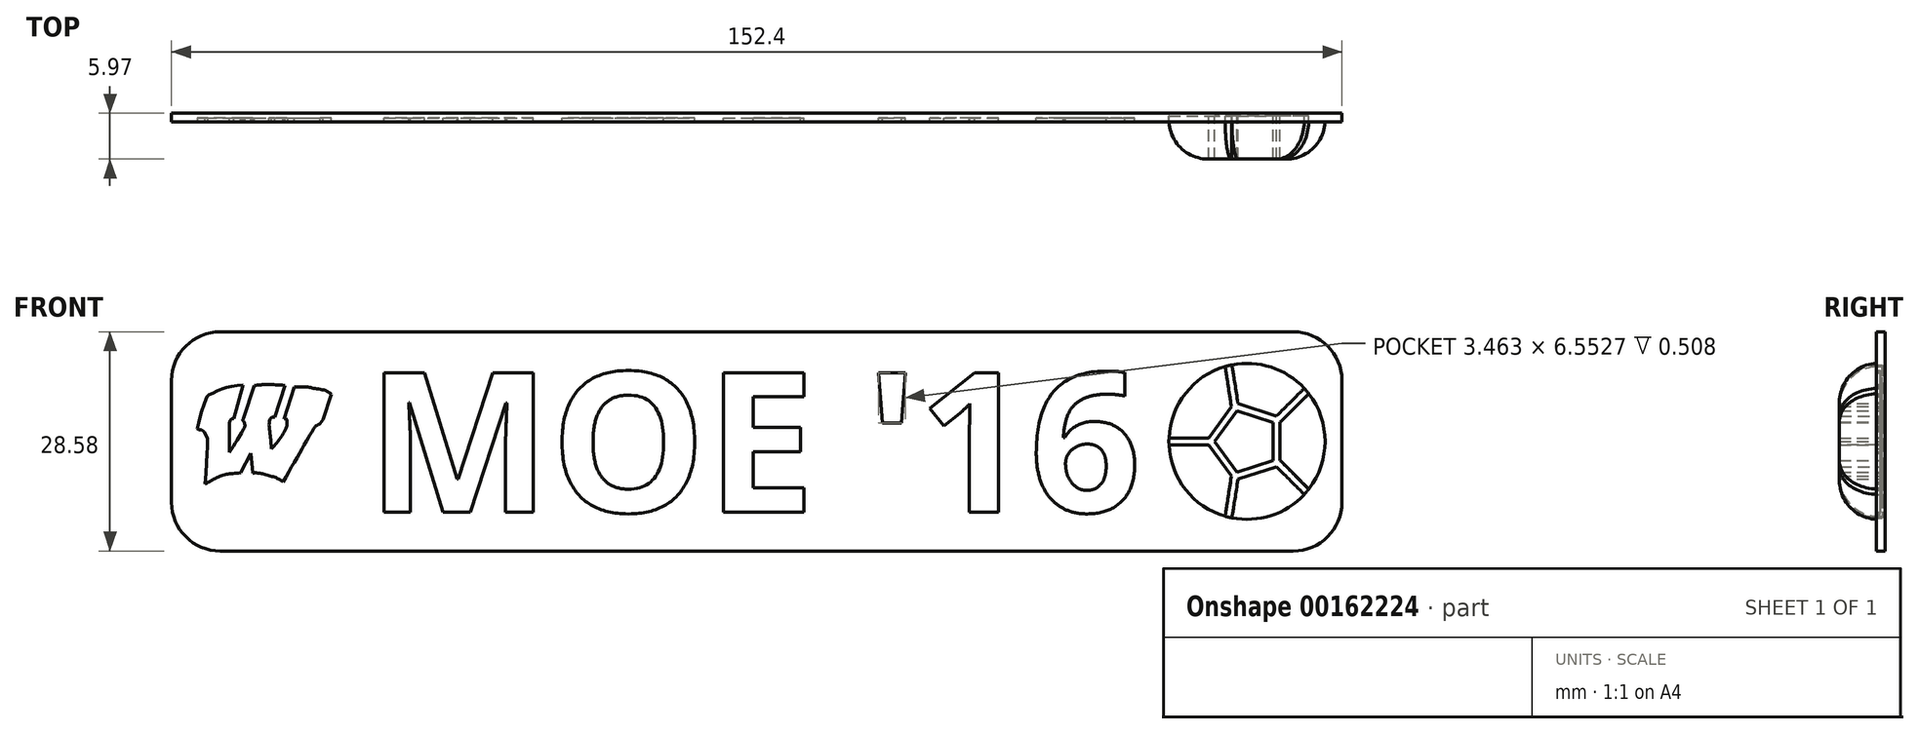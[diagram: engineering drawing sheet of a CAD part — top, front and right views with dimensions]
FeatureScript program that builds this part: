
annotation { "Feature Type Name" : "Feature", "Feature Type Description" : "" }
export const myFeature = defineFeature(function(context is Context, id is Id, definition is map)
    precondition{}
    {
        {
            var Q0;
            Q0=qCreatedBy(makeId("Front.planeOp"),FACE);
            var sketch = newSketch(context, id + "F0", { "sketchPlane" : qUnion([Q0])});
            skLineSegment(sketch, "E0.bottom", {"start": v(-52.2, 14.29) * mm, "end": v(87.5, 14.29) * mm});
            skLineSegment(sketch, "E0.top", {"start": v(-52.2, -14.29) * mm, "end": v(87.5, -14.29) * mm});
            skLineSegment(sketch, "E0.left", {"start": v(-58.55, 7.94) * mm, "end": v(-58.55, -7.94) * mm});
            skLineSegment(sketch, "E0.right", {"start": v(93.85, 7.94) * mm, "end": v(93.85, -7.94) * mm});
            skText(sketch, "E1", { "text": "MOE \'16", "fontName": "OpenSans-Bold.ttf"});
            skCircle(sketch, "E2", {"center": v(81.48, 0) * mm, "radius": 10.16 * mm});
            skCircle(sketch, "E3.cCircle", {"center": v(81.48, 0) * mm, "radius": 3.4 * mm, "construction": true});
            skLineSegment(sketch, "E3.0", {"start": v(84.88, 2.47) * mm, "end": v(84.88, -2.47) * mm});
            skLineSegment(sketch, "E3.1", {"start": v(84.88, -2.47) * mm, "end": v(80.18, -4) * mm});
            skLineSegment(sketch, "E3.2", {"start": v(80.18, -4) * mm, "end": v(77.27, 0) * mm});
            skLineSegment(sketch, "E3.3", {"start": v(77.27, 0) * mm, "end": v(80.18, 4) * mm});
            skLineSegment(sketch, "E3.4", {"start": v(80.18, 4) * mm, "end": v(84.88, 2.47) * mm});
            skPoint(sketch, "E3.0.midPoint", {"position": v(84.88, 0) * mm});
            skCircle(sketch, "E4.cCircle", {"center": v(81.48, 0) * mm, "radius": 4.32 * mm, "construction": true});
            skLineSegment(sketch, "E4.0", {"start": v(85.8, 3.14) * mm, "end": v(85.8, -3.14) * mm});
            skLineSegment(sketch, "E4.1", {"start": v(85.8, -3.14) * mm, "end": v(79.83, -5.08) * mm});
            skLineSegment(sketch, "E4.2", {"start": v(79.83, -5.08) * mm, "end": v(76.14, 0) * mm});
            skLineSegment(sketch, "E4.3", {"start": v(76.14, 0) * mm, "end": v(79.83, 5.08) * mm});
            skLineSegment(sketch, "E4.4", {"start": v(79.83, 5.08) * mm, "end": v(85.8, 3.14) * mm});
            skPoint(sketch, "E4.0.midPoint", {"position": v(85.8, 0) * mm});
            skLineSegment(sketch, "E5", {"start": v(85.8, 3.14) * mm, "end": v(89.23, 6.57) * mm, "construction": true});
            skLineSegment(sketch, "E6", {"start": v(85.8, -3.14) * mm, "end": v(89.23, -6.57) * mm, "construction": true});
            skLineSegment(sketch, "E7", {"start": v(76.14, 0) * mm, "end": v(71.32, 0) * mm, "construction": true});
            skLineSegment(sketch, "E8", {"start": v(79.83, 5.08) * mm, "end": v(79.07, 9.88) * mm, "construction": true});
            skLineSegment(sketch, "E9", {"start": v(79.83, -5.08) * mm, "end": v(79.07, -9.88) * mm, "construction": true});
            skLineSegment(sketch, "E10", {"start": v(79.45, 4.55) * mm, "end": v(78.63, 9.76) * mm});
            skLineSegment(sketch, "E11", {"start": v(79.52, 9.97) * mm, "end": v(80.32, 4.92) * mm});
            skLineSegment(sketch, "E12", {"start": v(71.33, 0.46) * mm, "end": v(76.48, 0.46) * mm});
            skLineSegment(sketch, "E13", {"start": v(71.33, -0.46) * mm, "end": v(76.48, -0.46) * mm});
            skLineSegment(sketch, "E14", {"start": v(79.45, -4.55) * mm, "end": v(78.63, -9.76) * mm});
            skPoint(sketch, "E14.startSnap0", {"position": v(79.45, -7.48) * mm});
            skLineSegment(sketch, "E15", {"start": v(80.32, -4.92) * mm, "end": v(79.52, -9.97) * mm});
            skLineSegment(sketch, "E16", {"start": v(88.93, -6.92) * mm, "end": v(85.31, -3.3) * mm});
            skLineSegment(sketch, "E17", {"start": v(89.52, -6.22) * mm, "end": v(85.8, -2.5) * mm});
            skLineSegment(sketch, "E18", {"start": v(85.8, 2.5) * mm, "end": v(89.52, 6.22) * mm});
            skLineSegment(sketch, "E19", {"start": v(85.31, 3.3) * mm, "end": v(88.93, 6.92) * mm});
            skPoint(sketch, "E20.visualSharp", {"position": v(93.85, 14.29) * mm});
            skArc(sketch, "E20.filletArc", {"start": v(93.85, 7.94) * mm, "mid": v(92, 12.43) * mm, "end": v(87.5, 14.29) * mm});
            skPoint(sketch, "E21.visualSharp", {"position": v(93.85, -14.29) * mm});
            skArc(sketch, "E21.filletArc", {"start": v(87.5, -14.29) * mm, "mid": v(92, -12.43) * mm, "end": v(93.85, -7.94) * mm});
            skPoint(sketch, "E22.visualSharp", {"position": v(-58.55, 14.29) * mm});
            skArc(sketch, "E22.filletArc", {"start": v(-52.2, 14.29) * mm, "mid": v(-56.69, 12.43) * mm, "end": v(-58.55, 7.94) * mm});
            skPoint(sketch, "E23.visualSharp", {"position": v(-58.55, -14.29) * mm});
            skArc(sketch, "E23.filletArc", {"start": v(-58.55, -7.94) * mm, "mid": v(-56.69, -12.43) * mm, "end": v(-52.2, -14.29) * mm});
            skFitSpline(sketch, "E24", {"points": [v(-49.22, 7.36) * mm, v(-51.14, 7.07) * mm, v(-52.41, 6.66) * mm, v(-53.63, 6.08) * mm, v(-54.04, 5.65) * mm, v(-55.17, 1.56) * mm, v(-55.05, 1.53) * mm, v(-54.68, 1.5) * mm, v(-54.21, 1.1) * mm, v(-53.9, 0.34) * mm, v(-53.86, -0.6) * mm, v(-54.17, -5.57) * mm], "startDerivative": vector(-18.16, -2.3) * mm, "endDerivative": vector(-2.14, -33.25) * mm});
            skFitSpline(sketch, "E25", {"points": [v(-54.17, -5.57) * mm, v(-53.65, -5.26) * mm, v(-53.07, -4.93) * mm, v(-52.29, -4.57) * mm, v(-51.44, -4.3) * mm, v(-50.68, -4.19) * mm, v(-49.58, -4.1) * mm], "startDerivative": vector(3.4, 2.8) * mm, "endDerivative": vector(6, 0.4) * mm});
            skLineSegment(sketch, "E26", {"start": v(-49.58, -4.1) * mm, "end": v(-48.22, -1.53) * mm});
            skLineSegment(sketch, "E27", {"start": v(-48.22, -1.53) * mm, "end": v(-47.98, -4.12) * mm});
            skFitSpline(sketch, "E28", {"points": [v(-47.98, -4.12) * mm, v(-47.32, -4.12) * mm, v(-46.58, -4.24) * mm, v(-45.54, -4.54) * mm, v(-44.68, -4.86) * mm, v(-44.02, -5.28) * mm], "startDerivative": vector(3.67, 0.12) * mm, "endDerivative": vector(3.24, -2.36) * mm});
            skFitSpline(sketch, "E29", {"points": [v(-44.02, -5.28) * mm, v(-39.97, 1.74) * mm, v(-39.73, 2.03) * mm, v(-39.46, 2.18) * mm, v(-39.19, 2.35) * mm], "startDerivative": vector(8.56, 15.03) * mm, "endDerivative": vector(2.11, 1.44) * mm});
            skLineSegment(sketch, "E30", {"start": v(-39.19, 2.35) * mm, "end": v(-38.85, 2.82) * mm});
            skLineSegment(sketch, "E31", {"start": v(-38.85, 2.82) * mm, "end": v(-37.74, 6.16) * mm});
            skLineSegment(sketch, "E32", {"start": v(-42.55, 7.06) * mm, "end": v(-43.92, 2.93) * mm});
            skLineSegment(sketch, "E33", {"start": v(-43.78, 7.27) * mm, "end": v(-45.08, 3.15) * mm});
            skLineSegment(sketch, "E34", {"start": v(-49.22, 7.36) * mm, "end": v(-50.44, 2.95) * mm});
            skLineSegment(sketch, "E35", {"start": v(-47.78, 7.27) * mm, "end": v(-49.17, 3.01) * mm});
            skLineSegment(sketch, "E36", {"start": v(-51, 2.4) * mm, "end": v(-51, -1.44) * mm});
            skFitSpline(sketch, "E37", {"points": [v(-51, 2.4) * mm, v(-50.93, 2.7) * mm, v(-50.79, 2.86) * mm, v(-50.62, 2.96) * mm, v(-50.44, 2.95) * mm], "startDerivative": vector(0.1, 1.13) * mm, "endDerivative": vector(0.8, -0.18) * mm});
            skFitSpline(sketch, "E38", {"points": [v(-51, -1.44) * mm, v(-49.08, 1.76) * mm, v(-49, 2.04) * mm, v(-49.03, 2.3) * mm, v(-49.22, 2.68) * mm, v(-49.28, 2.8) * mm, v(-49.17, 3.01) * mm], "startDerivative": vector(5.88, 9.47) * mm, "endDerivative": vector(1.55, 2.17) * mm});
            skFitSpline(sketch, "E39", {"points": [v(-45.08, 3.15) * mm, v(-45.28, 3.15) * mm, v(-45.41, 3.15) * mm, v(-45.76, 2.8) * mm, v(-45.7, 0.74) * mm, v(-45.53, -0.95) * mm], "startDerivative": vector(-1.81, -0.11) * mm, "endDerivative": vector(0.55, -5.24) * mm});
            skFitSpline(sketch, "E40", {"points": [v(-43.92, 2.93) * mm, v(-43.6, 2.93) * mm, v(-43.49, 2.47) * mm, v(-43.57, 1.85) * mm, v(-44.45, 0.32) * mm, v(-45.53, -0.95) * mm], "startDerivative": vector(2.79, 0.73) * mm, "endDerivative": vector(-3.92, -4.22) * mm});
            skFitSpline(sketch, "E41", {"points": [v(-47.78, 7.27) * mm, v(-46.38, 7.39) * mm, v(-43.78, 7.27) * mm], "startDerivative": vector(4.88, 0.78) * mm, "endDerivative": vector(4.26, -0.68) * mm});
            skFitSpline(sketch, "E42", {"points": [v(-42.55, 7.06) * mm, v(-40.8, 7.08) * mm, v(-39.86, 6.9) * mm, v(-38.5, 6.61) * mm, v(-37.74, 6.16) * mm], "startDerivative": vector(10.06, 0.33) * mm, "endDerivative": vector(3.23, -2.15) * mm});
            const initialGuessF0  = {"E1": [-0.03315, -0.0092, 1, 0, 0.0183]};
            skSetInitialGuess(sketch, initialGuessF0);
            skSolve(sketch);
        }
        {
            var Q0;
            Q0 = qSketchRegion(id + "F0", true);
            var Q1;
            Q1=makeQuery(id+"F0.imprint","IMPRINT",FACE,{"disambiguationData":[TD([[makeQuery(id+"F0.imprint","IMPRINT",EDGE,{"derivedFrom":sQuery(id+"F0.wireOp",EDGE,"E0.bottom")}),-1.0]])]});
            var Q2;
            {var subQ0=sQuery(id+"F0.wireOp",EDGE,"E13");Q2=makeQuery(id+"F0.imprint","IMPRINT",FACE,{"disambiguationData":[TD([[makeQuery(id+"F0.imprint","IMPRINT",EDGE,{"derivedFrom":subQ0}),-1.0]])]});}
            var Q3;
            {var subQ0=sQuery(id+"F0.wireOp",EDGE,"E10");Q3=makeQuery(id+"F0.imprint","IMPRINT",FACE,{"disambiguationData":[TD([[makeQuery(id+"F0.imprint","IMPRINT",EDGE,{"derivedFrom":subQ0}),1.0]])]});}
            var Q4;
            Q4=makeQuery(id+"F0.imprint","IMPRINT",FACE,{"disambiguationData":[TD([[makeQuery(id+"F0.imprint","IMPRINT",EDGE,{"derivedFrom":sQuery(id+"F0.wireOp",EDGE,"E1.sketch_text.stroke-0")}),-1.0]])]});
            var Q5;
            Q5=makeQuery(id+"F0.imprint","IMPRINT",FACE,{"disambiguationData":[TD([[makeQuery(id+"F0.imprint","IMPRINT",EDGE,{"derivedFrom":sQuery(id+"F0.wireOp",EDGE,"E1.sketch_text.stroke-33")}),-1.0]])]});
            var Q6;
            Q6=makeQuery(id+"F0.imprint","IMPRINT",FACE,{"disambiguationData":[TD([[makeQuery(id+"F0.imprint","IMPRINT",EDGE,{"derivedFrom":sQuery(id+"F0.wireOp",EDGE,"E1.sketch_text.stroke-45")}),-1.0]])]});
            var Q7;
            Q7=makeQuery(id+"F0.imprint","IMPRINT",FACE,{"disambiguationData":[TD([[makeQuery(id+"F0.imprint","IMPRINT",EDGE,{"derivedFrom":sQuery(id+"F0.wireOp",EDGE,"E1.sketch_text.stroke-49")}),-1.0]])]});
            var Q8;
            Q8=makeQuery(id+"F0.imprint","IMPRINT",FACE,{"disambiguationData":[TD([[makeQuery(id+"F0.imprint","IMPRINT",EDGE,{"derivedFrom":sQuery(id+"F0.wireOp",EDGE,"E1.sketch_text.stroke-76")}),1.0]])]});
            var Q9;
            Q9=makeQuery(id+"F0.imprint","IMPRINT",FACE,{"disambiguationData":[TD([[makeQuery(id+"F0.imprint","IMPRINT",EDGE,{"derivedFrom":sQuery(id+"F0.wireOp",EDGE,"E1.sketch_text.stroke-19")}),-1.0]])]});
            var Q10;
            Q10=makeQuery(id+"F0.imprint","IMPRINT",FACE,{"disambiguationData":[TD([[makeQuery(id+"F0.imprint","IMPRINT",EDGE,{"derivedFrom":sQuery(id+"F0.wireOp",EDGE,"E1.sketch_text.stroke-59")}),-1.0]])]});
            var Q11;
            {var subQ0=sQuery(id+"F0.wireOp",EDGE,"E11");Q11=makeQuery(id+"F0.imprint","IMPRINT",FACE,{"disambiguationData":[TD([[makeQuery(id+"F0.imprint","IMPRINT",EDGE,{"derivedFrom":subQ0}),1.0]])]});}
            var Q12;
            {var subQ0=sQuery(id+"F0.wireOp",EDGE,"E17");Q12=makeQuery(id+"F0.imprint","IMPRINT",FACE,{"disambiguationData":[TD([[makeQuery(id+"F0.imprint","IMPRINT",EDGE,{"derivedFrom":subQ0}),-1.0]])]});}
            var Q13;
            Q13=makeQuery(id+"F0.imprint","IMPRINT",FACE,{"disambiguationData":[TD([[makeQuery(id+"F0.imprint","IMPRINT",EDGE,{"derivedFrom":sQuery(id+"F0.wireOp",EDGE,"E1.sketch_text.stroke-27")}),1.0]])]});
            var Q14;
            Q14=makeQuery(id+"F0.imprint","IMPRINT",FACE,{"disambiguationData":[TD([[makeQuery(id+"F0.imprint","IMPRINT",EDGE,{"derivedFrom":sQuery(id+"F0.wireOp",EDGE,"E24")}),1.0]])]});
            var Q15;
            {var subQ0=sQuery(id+"F0.wireOp",EDGE,"E15");Q15=makeQuery(id+"F0.imprint","IMPRINT",FACE,{"disambiguationData":[TD([[makeQuery(id+"F0.imprint","IMPRINT",EDGE,{"derivedFrom":subQ0}),1.0]])]});}
            var Q16;
            {var subQ0=sQuery(id+"F0.wireOp",EDGE,"E16");Q16=makeQuery(id+"F0.imprint","IMPRINT",FACE,{"disambiguationData":[TD([[makeQuery(id+"F0.imprint","IMPRINT",EDGE,{"derivedFrom":subQ0}),-1.0]])]});}
            var Q17;
            {var subQ0=sQuery(id+"F0.wireOp",EDGE,"E14");Q17=makeQuery(id+"F0.imprint","IMPRINT",FACE,{"disambiguationData":[TD([[makeQuery(id+"F0.imprint","IMPRINT",EDGE,{"derivedFrom":subQ0}),1.0]])]});}
            var Q18;
            {var subQ0=sQuery(id+"F0.wireOp",EDGE,"E18");Q18=makeQuery(id+"F0.imprint","IMPRINT",FACE,{"disambiguationData":[TD([[makeQuery(id+"F0.imprint","IMPRINT",EDGE,{"derivedFrom":subQ0}),1.0]])]});}
            var Q19;
            {var subQ0=sQuery(id+"F0.wireOp",EDGE,"E10");Q19=makeQuery(id+"F0.imprint","IMPRINT",FACE,{"disambiguationData":[TD([[makeQuery(id+"F0.imprint","IMPRINT",EDGE,{"derivedFrom":subQ0}),-1.0]])]});}
            var Q20;
            Q20=makeQuery(id+"F0.imprint","IMPRINT",FACE,{"disambiguationData":[TD([[makeQuery(id+"F0.imprint","IMPRINT",EDGE,{"derivedFrom":sQuery(id+"F0.wireOp",EDGE,"E3.0")}),1.0]])]});
            var Q21;
            {var subQ0=sQuery(id+"F0.wireOp",EDGE,"E12");Q21=makeQuery(id+"F0.imprint","IMPRINT",FACE,{"disambiguationData":[TD([[makeQuery(id+"F0.imprint","IMPRINT",EDGE,{"derivedFrom":subQ0}),-1.0]])]});}
            var Q22;
            Q22=makeQuery(id+"F0.imprint","IMPRINT",FACE,{"disambiguationData":[TD([[makeQuery(id+"F0.imprint","IMPRINT",EDGE,{"derivedFrom":sQuery(id+"F0.wireOp",EDGE,"E3.0")}),-1.0]])]});
            extrude(context, id + "F1", {"entities" : qUnion([Q0, Q1, Q2, Q3, Q4, Q5, Q6, Q7, Q8, Q9, Q10, Q11, Q12, Q13, Q14, Q15, Q16, Q17, Q18, Q19, Q20, Q21, Q22]), "depth" : 0.25 * mm, "hasSecondDirection" : true, "secondDirectionOppositeDirection" : true, "secondDirectionDepth" : 0.38 * mm});
        }
        {
            var Q0;
            Q0 = qSketchRegion(id + "F0", true);
            var Q1;
            Q1=makeQuery(id+"F0.imprint","IMPRINT",FACE,{"disambiguationData":[TD([[makeQuery(id+"F0.imprint","IMPRINT",EDGE,{"derivedFrom":sQuery(id+"F0.wireOp",EDGE,"E1.sketch_text.stroke-76")}),1.0]])]});
            var Q2;
            Q2=makeQuery(id+"F0.imprint","IMPRINT",FACE,{"disambiguationData":[TD([[makeQuery(id+"F0.imprint","IMPRINT",EDGE,{"derivedFrom":sQuery(id+"F0.wireOp",EDGE,"E1.sketch_text.stroke-27")}),1.0]])]});
            extrude(context, id + "F2", {"entities" : qUnion([Q0, Q1, Q2]), "operationType" : NewBodyOperationType.ADD, "depth" : 0.76 * mm});
        }
        {
            var Q0;
            {var subQ0=sQuery(id+"F0.wireOp",EDGE,"E10");Q0=makeQuery(id+"F0.imprint","IMPRINT",FACE,{"disambiguationData":[TD([[makeQuery(id+"F0.imprint","IMPRINT",EDGE,{"derivedFrom":subQ0}),-1.0]])]});}
            var Q1;
            Q1=makeQuery(id+"F0.imprint","IMPRINT",FACE,{"disambiguationData":[TD([[makeQuery(id+"F0.imprint","IMPRINT",EDGE,{"derivedFrom":sQuery(id+"F0.wireOp",EDGE,"E3.0")}),1.0]])]});
            var Q2;
            {var subQ0=sQuery(id+"F0.wireOp",EDGE,"E12");Q2=makeQuery(id+"F0.imprint","IMPRINT",FACE,{"disambiguationData":[TD([[makeQuery(id+"F0.imprint","IMPRINT",EDGE,{"derivedFrom":subQ0}),-1.0]])]});}
            var Q3;
            {var subQ0=sQuery(id+"F0.wireOp",EDGE,"E18");Q3=makeQuery(id+"F0.imprint","IMPRINT",FACE,{"disambiguationData":[TD([[makeQuery(id+"F0.imprint","IMPRINT",EDGE,{"derivedFrom":subQ0}),1.0]])]});}
            var Q4;
            {var subQ0=sQuery(id+"F0.wireOp",EDGE,"E16");Q4=makeQuery(id+"F0.imprint","IMPRINT",FACE,{"disambiguationData":[TD([[makeQuery(id+"F0.imprint","IMPRINT",EDGE,{"derivedFrom":subQ0}),-1.0]])]});}
            var Q5;
            {var subQ0=sQuery(id+"F0.wireOp",EDGE,"E14");Q5=makeQuery(id+"F0.imprint","IMPRINT",FACE,{"disambiguationData":[TD([[makeQuery(id+"F0.imprint","IMPRINT",EDGE,{"derivedFrom":subQ0}),1.0]])]});}
            extrude(context, id + "F3", {"entities" : qUnion([Q0, Q1, Q2, Q3, Q4, Q5]), "operationType" : NewBodyOperationType.REMOVE, "depth" : 0.5 * mm});
        }
        {
            var Q0;
            Q0=makeQuery(id+"F2.boolean.opBoolean","SPLIT",FACE,{"disambiguationData":[TD([makeQuery(id+"F2.opExtrude","SWEPT_FACE",FACE,{"disambiguationData":[OSD([sQuery(id+"F0.wireOp",EDGE,"E2")])]})])],"derivedFrom":makeQuery(id+"F1.opExtrude","CAP_FACE",FACE,{"disambiguationData":[OSD([sQuery(id+"F0.wireOp",EDGE,"E0.bottom"),sQuery(id+"F0.wireOp",EDGE,"E0.top"),sQuery(id+"F0.wireOp",EDGE,"E0.left"),sQuery(id+"F0.wireOp",EDGE,"E0.right"),sQuery(id+"F0.wireOp",EDGE,"E20.filletArc"),sQuery(id+"F0.wireOp",EDGE,"E21.filletArc"),sQuery(id+"F0.wireOp",EDGE,"E22.filletArc"),sQuery(id+"F0.wireOp",EDGE,"E23.filletArc")])],"isStart":false})});
            extrude(context, id + "F4", {"entities" : qUnion([Q0]), "operationType" : NewBodyOperationType.ADD, "depth" : 5.33 * mm});
        }
        {
            var Q0;
            {var subQ0=sQuery(id+"F0.wireOp",EDGE,"E2");var subQ1=sQuery(id+"F0.wireOp",EDGE,"E13");var subQ2=makeQuery(id+"F2.opExtrude","SWEPT_FACE",FACE,{"disambiguationData":[OSD([subQ0])]});var subQ4=sQuery(id+"F0.wireOp",EDGE,"E23.filletArc");var subQ5=sQuery(id+"F0.wireOp",EDGE,"E22.filletArc");var subQ6=sQuery(id+"F0.wireOp",EDGE,"E21.filletArc");var subQ7=sQuery(id+"F0.wireOp",EDGE,"E20.filletArc");var subQ8=sQuery(id+"F0.wireOp",EDGE,"E0.right");var subQ9=sQuery(id+"F0.wireOp",EDGE,"E0.left");var subQ10=sQuery(id+"F0.wireOp",EDGE,"E0.top");var subQ11=sQuery(id+"F0.wireOp",EDGE,"E0.bottom");var subQ12=makeQuery(id+"F1.opExtrude","CAP_FACE",FACE,{"disambiguationData":[OSD([subQ11,subQ10,subQ9,subQ8,subQ7,subQ6,subQ5,subQ4])],"isStart":false});Q0=makeQuery(id+"F4.opExtrude","CAP_EDGE",EDGE,{"disambiguationData":[OSD([subQ11,subQ10,subQ9,subQ8,subQ0,subQ7,subQ6,subQ5,subQ4]),TDD([makeQuery(id+"F3.boolean.opBoolean","SPLIT",EDGE,{"disambiguationData":[TD([makeQuery(id+"F3.opExtrude","SWEPT_FACE",FACE,{"disambiguationData":[OSD([subQ1])]})])],"derivedFrom":makeQuery(id+"F2.boolean.opBoolean","INTERSECT",EDGE,{"derivedFrom":[subQ12,subQ2]})})])],"isStart":false});}
            var Q1;
            {var subQ0=sQuery(id+"F0.wireOp",EDGE,"E2");var subQ1=makeQuery(id+"F2.opExtrude","SWEPT_FACE",FACE,{"disambiguationData":[OSD([subQ0])]});var subQ2=sQuery(id+"F0.wireOp",EDGE,"E15");var subQ3=sQuery(id+"F0.wireOp",EDGE,"E23.filletArc");var subQ4=sQuery(id+"F0.wireOp",EDGE,"E22.filletArc");var subQ5=sQuery(id+"F0.wireOp",EDGE,"E21.filletArc");var subQ6=sQuery(id+"F0.wireOp",EDGE,"E20.filletArc");var subQ7=sQuery(id+"F0.wireOp",EDGE,"E0.right");var subQ8=sQuery(id+"F0.wireOp",EDGE,"E0.left");var subQ9=sQuery(id+"F0.wireOp",EDGE,"E0.top");var subQ10=sQuery(id+"F0.wireOp",EDGE,"E0.bottom");var subQ11=makeQuery(id+"F1.opExtrude","CAP_FACE",FACE,{"disambiguationData":[OSD([subQ10,subQ9,subQ8,subQ7,subQ6,subQ5,subQ4,subQ3])],"isStart":false});Q1=makeQuery(id+"F4.opExtrude","CAP_EDGE",EDGE,{"disambiguationData":[OSD([subQ10,subQ9,subQ8,subQ7,subQ0,subQ6,subQ5,subQ4,subQ3]),TDD([makeQuery(id+"F3.boolean.opBoolean","SPLIT",EDGE,{"disambiguationData":[TD([makeQuery(id+"F3.opExtrude","SWEPT_FACE",FACE,{"disambiguationData":[OSD([subQ2])]})])],"derivedFrom":makeQuery(id+"F2.boolean.opBoolean","INTERSECT",EDGE,{"derivedFrom":[subQ11,subQ1]})})])],"isStart":false});}
            var Q2;
            {var subQ0=sQuery(id+"F0.wireOp",EDGE,"E2");var subQ1=sQuery(id+"F0.wireOp",EDGE,"E17");var subQ3=makeQuery(id+"F2.opExtrude","SWEPT_FACE",FACE,{"disambiguationData":[OSD([subQ0])]});var subQ4=sQuery(id+"F0.wireOp",EDGE,"E23.filletArc");var subQ5=sQuery(id+"F0.wireOp",EDGE,"E22.filletArc");var subQ6=sQuery(id+"F0.wireOp",EDGE,"E21.filletArc");var subQ7=sQuery(id+"F0.wireOp",EDGE,"E20.filletArc");var subQ8=sQuery(id+"F0.wireOp",EDGE,"E0.right");var subQ9=sQuery(id+"F0.wireOp",EDGE,"E0.left");var subQ10=sQuery(id+"F0.wireOp",EDGE,"E0.top");var subQ11=sQuery(id+"F0.wireOp",EDGE,"E0.bottom");var subQ12=makeQuery(id+"F1.opExtrude","CAP_FACE",FACE,{"disambiguationData":[OSD([subQ11,subQ10,subQ9,subQ8,subQ7,subQ6,subQ5,subQ4])],"isStart":false});Q2=makeQuery(id+"F4.opExtrude","CAP_EDGE",EDGE,{"disambiguationData":[OSD([subQ11,subQ10,subQ9,subQ8,subQ0,subQ7,subQ6,subQ5,subQ4]),TDD([makeQuery(id+"F3.boolean.opBoolean","SPLIT",EDGE,{"disambiguationData":[TD([makeQuery(id+"F3.opExtrude","SWEPT_FACE",FACE,{"disambiguationData":[OSD([subQ1])]})])],"derivedFrom":makeQuery(id+"F2.boolean.opBoolean","INTERSECT",EDGE,{"derivedFrom":[subQ12,subQ3]})})])],"isStart":false});}
            var Q3;
            {var subQ0=sQuery(id+"F0.wireOp",EDGE,"E2");var subQ1=sQuery(id+"F0.wireOp",EDGE,"E11");var subQ3=makeQuery(id+"F2.opExtrude","SWEPT_FACE",FACE,{"disambiguationData":[OSD([subQ0])]});var subQ4=sQuery(id+"F0.wireOp",EDGE,"E23.filletArc");var subQ5=sQuery(id+"F0.wireOp",EDGE,"E22.filletArc");var subQ6=sQuery(id+"F0.wireOp",EDGE,"E21.filletArc");var subQ7=sQuery(id+"F0.wireOp",EDGE,"E20.filletArc");var subQ8=sQuery(id+"F0.wireOp",EDGE,"E0.right");var subQ9=sQuery(id+"F0.wireOp",EDGE,"E0.left");var subQ10=sQuery(id+"F0.wireOp",EDGE,"E0.top");var subQ11=sQuery(id+"F0.wireOp",EDGE,"E0.bottom");var subQ12=makeQuery(id+"F1.opExtrude","CAP_FACE",FACE,{"disambiguationData":[OSD([subQ11,subQ10,subQ9,subQ8,subQ7,subQ6,subQ5,subQ4])],"isStart":false});Q3=makeQuery(id+"F4.opExtrude","CAP_EDGE",EDGE,{"disambiguationData":[OSD([subQ11,subQ10,subQ9,subQ8,subQ0,subQ7,subQ6,subQ5,subQ4]),TDD([makeQuery(id+"F3.boolean.opBoolean","SPLIT",EDGE,{"disambiguationData":[TD([makeQuery(id+"F3.opExtrude","SWEPT_FACE",FACE,{"disambiguationData":[OSD([subQ1])]})])],"derivedFrom":makeQuery(id+"F2.boolean.opBoolean","INTERSECT",EDGE,{"derivedFrom":[subQ12,subQ3]})})])],"isStart":false});}
            var Q4;
            {var subQ0=sQuery(id+"F0.wireOp",EDGE,"E10");var subQ1=sQuery(id+"F0.wireOp",EDGE,"E2");var subQ2=makeQuery(id+"F2.opExtrude","SWEPT_FACE",FACE,{"disambiguationData":[OSD([subQ1])]});var subQ3=sQuery(id+"F0.wireOp",EDGE,"E23.filletArc");var subQ4=sQuery(id+"F0.wireOp",EDGE,"E22.filletArc");var subQ5=sQuery(id+"F0.wireOp",EDGE,"E21.filletArc");var subQ6=sQuery(id+"F0.wireOp",EDGE,"E20.filletArc");var subQ7=sQuery(id+"F0.wireOp",EDGE,"E0.right");var subQ8=sQuery(id+"F0.wireOp",EDGE,"E0.left");var subQ9=sQuery(id+"F0.wireOp",EDGE,"E0.top");var subQ10=sQuery(id+"F0.wireOp",EDGE,"E0.bottom");var subQ11=makeQuery(id+"F1.opExtrude","CAP_FACE",FACE,{"disambiguationData":[OSD([subQ10,subQ9,subQ8,subQ7,subQ6,subQ5,subQ4,subQ3])],"isStart":false});Q4=makeQuery(id+"F4.opExtrude","CAP_EDGE",EDGE,{"disambiguationData":[OSD([subQ10,subQ9,subQ8,subQ7,subQ1,subQ6,subQ5,subQ4,subQ3]),TDD([makeQuery(id+"F3.boolean.opBoolean","SPLIT",EDGE,{"disambiguationData":[TD([makeQuery(id+"F3.opExtrude","SWEPT_FACE",FACE,{"disambiguationData":[OSD([subQ0])]})])],"derivedFrom":makeQuery(id+"F2.boolean.opBoolean","INTERSECT",EDGE,{"derivedFrom":[subQ11,subQ2]})})])],"isStart":false});}
            fillet(context, id + "F5", {"entities" : qUnion([Q0, Q1, Q2, Q3, Q4]), "radius" : 5.08 * mm, "tangentPropagation" : true, "allowEdgeOverflow" : false});
        }
    });
